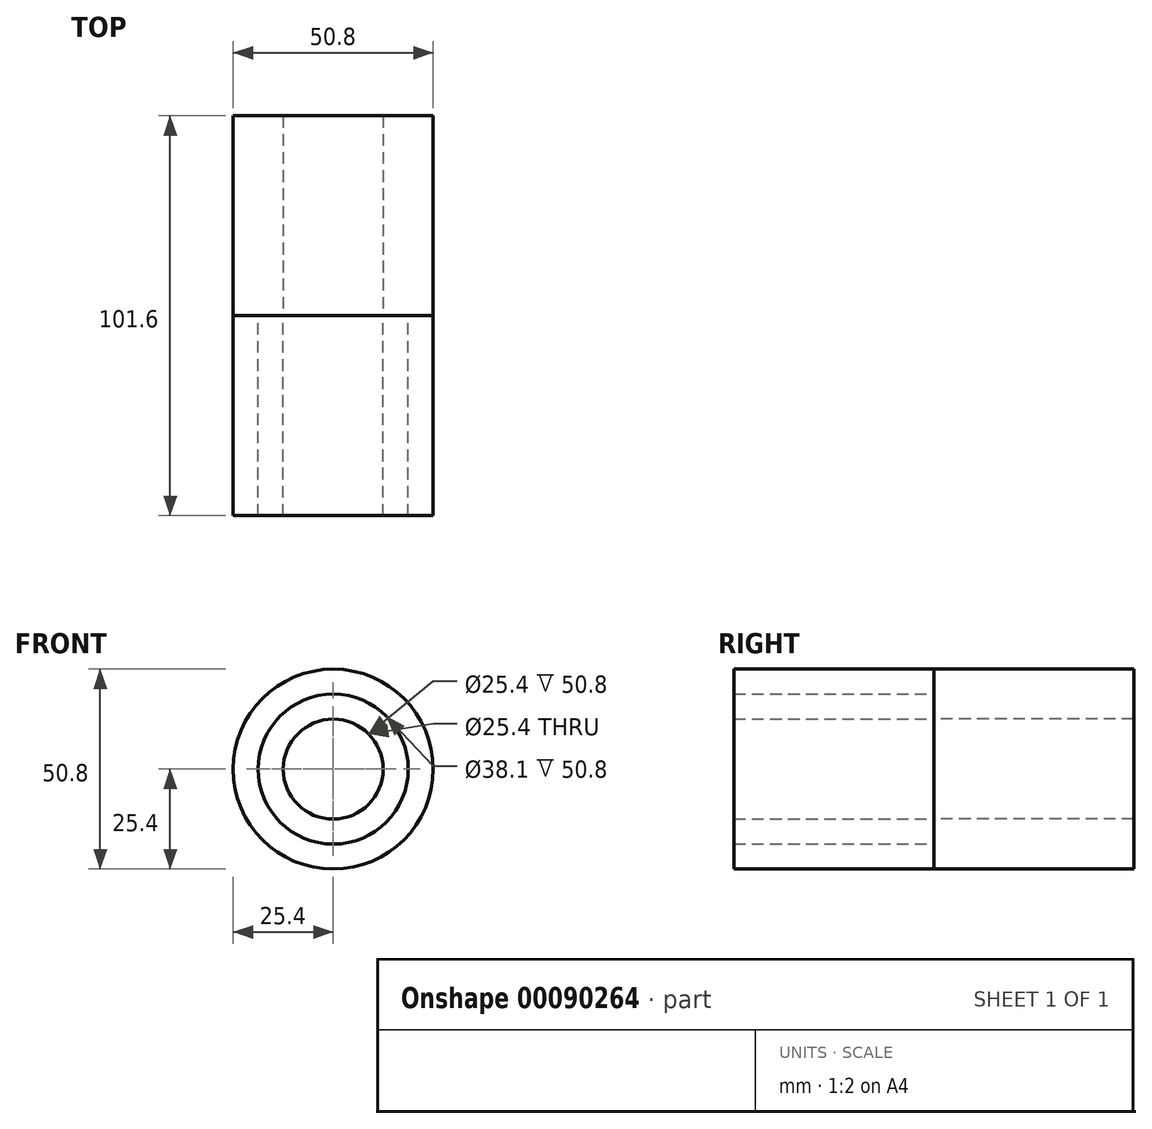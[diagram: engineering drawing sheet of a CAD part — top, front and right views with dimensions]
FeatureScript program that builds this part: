
annotation { "Feature Type Name" : "Feature", "Feature Type Description" : "" }
export const myFeature = defineFeature(function(context is Context, id is Id, definition is map)
    precondition{}
    {
        {
            var Q0;
            Q0=qCreatedBy(makeId("Front.planeOp"),FACE);
            var sketch = newSketch(context, id + "F0", { "sketchPlane" : qUnion([Q0])});
            skCircle(sketch, "E0", {"center": v(0, 0) * mm, "radius": 19.05 * mm});
            skCircle(sketch, "E1.0", {"center": v(0, 0) * mm, "radius": 25.4 * mm});
            skCircle(sketch, "E2", {"center": v(0, 0) * mm, "radius": 12.7 * mm});
            skSolve(sketch);
        }
        {
            var Q0;
            Q0=makeQuery(id+"F0.imprint","IMPRINT",FACE,{"disambiguationData":[TD([[makeQuery(id+"F0.imprint","IMPRINT",EDGE,{"derivedFrom":sQuery(id+"F0.wireOp",EDGE,"E0")}),-1.0]])]});
            extrude(context, id + "F1", {"entities" : qUnion([Q0]), "depth" : 50.8 * mm});
        }
        {
            var Q0;
            Q0=makeQuery(id+"F0.imprint","IMPRINT",FACE,{"disambiguationData":[TD([[makeQuery(id+"F0.imprint","IMPRINT",EDGE,{"derivedFrom":sQuery(id+"F0.wireOp",EDGE,"E0")}),1.0]])]});
            extrude(context, id + "F2", {"entities" : qUnion([Q0]), "depth" : 50.8 * mm});
        }
        {
            var Q0;
            Q0=makeQuery(id+"F0.imprint","IMPRINT",FACE,{"disambiguationData":[TD([[makeQuery(id+"F0.imprint","IMPRINT",EDGE,{"derivedFrom":sQuery(id+"F0.wireOp",EDGE,"E0")}),1.0]])]});
            var Q1;
            Q1=makeQuery(id+"F0.imprint","IMPRINT",FACE,{"disambiguationData":[TD([[makeQuery(id+"F0.imprint","IMPRINT",EDGE,{"derivedFrom":sQuery(id+"F0.wireOp",EDGE,"E0")}),-1.0]])]});
            extrude(context, id + "F3", {"entities" : qUnion([Q0, Q1]), "oppositeDirection" : true, "depth" : 50.8 * mm});
        }
    });
